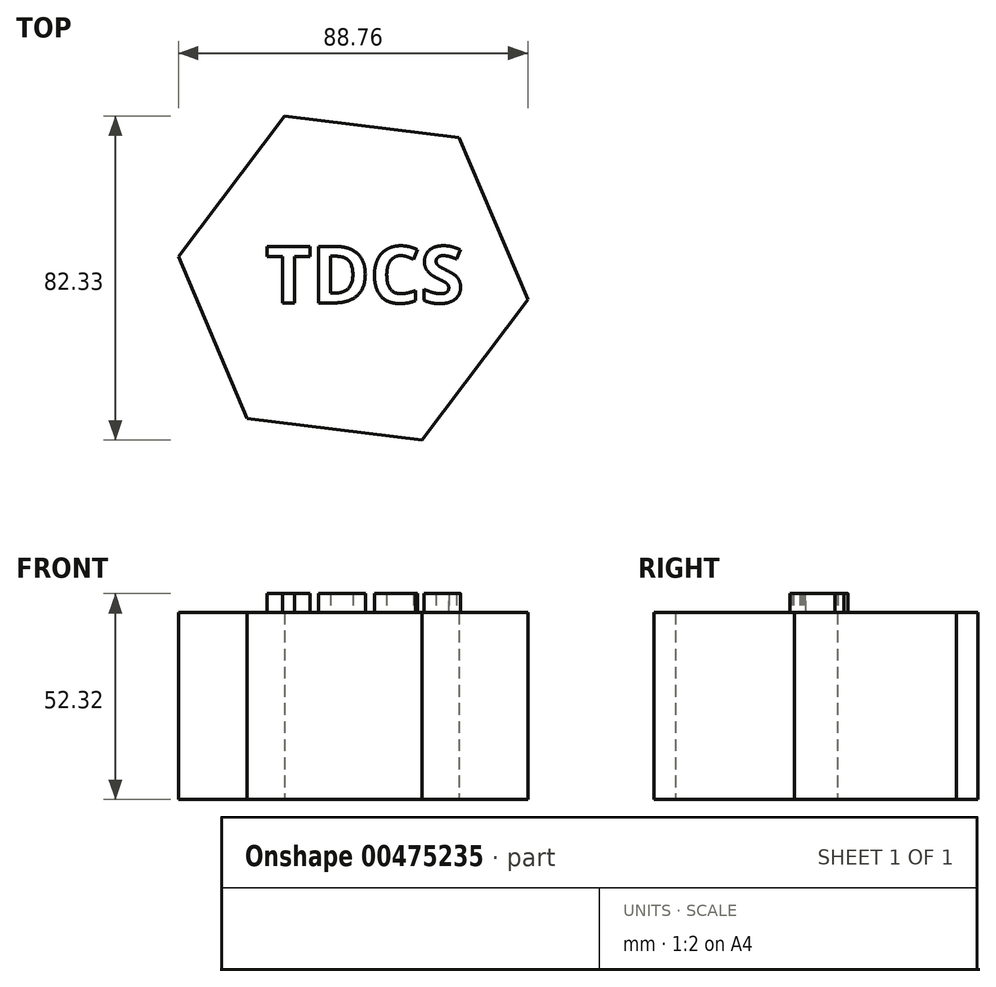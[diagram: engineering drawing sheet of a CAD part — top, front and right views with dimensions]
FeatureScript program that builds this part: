
annotation { "Feature Type Name" : "Feature", "Feature Type Description" : "" }
export const myFeature = defineFeature(function(context is Context, id is Id, definition is map)
    precondition{}
    {
        {
            var Q0;
            Q0=qCreatedBy(makeId("Top.planeOp"),FACE);
            var sketch = newSketch(context, id + "F0", { "sketchPlane" : qUnion([Q0])});
            skCircle(sketch, "E0.cCircle", {"center": v(-33.68, 25.98) * mm, "radius": 38.73 * mm, "construction": true});
            skLineSegment(sketch, "E0.0", {"start": v(10.7, 20.51) * mm, "end": v(-16.22, -15.2) * mm});
            skLineSegment(sketch, "E0.1", {"start": v(-16.22, -15.2) * mm, "end": v(-60.6, -9.73) * mm});
            skLineSegment(sketch, "E0.2", {"start": v(-60.6, -9.73) * mm, "end": v(-78.06, 31.44) * mm});
            skLineSegment(sketch, "E0.3", {"start": v(-78.06, 31.44) * mm, "end": v(-51.14, 67.14) * mm});
            skLineSegment(sketch, "E0.4", {"start": v(-51.14, 67.14) * mm, "end": v(-6.76, 61.68) * mm});
            skLineSegment(sketch, "E0.5", {"start": v(-6.76, 61.68) * mm, "end": v(10.7, 20.51) * mm});
            skPoint(sketch, "E0.0.midPoint", {"position": v(-2.76, 2.66) * mm});
            skSolve(sketch);
        }
        {
            var Q0;
            Q0=makeQuery(id+"F0.imprint","IMPRINT",FACE,{"disambiguationData":[TD([[makeQuery(id+"F0.imprint","IMPRINT",EDGE,{"derivedFrom":sQuery(id+"F0.wireOp",EDGE,"E0.0")}),-1.0]])]});
            extrude(context, id + "F1", {"entities" : qUnion([Q0]), "depth" : 47.5 * mm});
        }
        {
            var Q0;
            Q0=makeQuery(id+"F1.opExtrude","CAP_FACE",FACE,{"disambiguationData":[OSD([sQuery(id+"F0.wireOp",EDGE,"E0.0"),sQuery(id+"F0.wireOp",EDGE,"E0.1"),sQuery(id+"F0.wireOp",EDGE,"E0.2"),sQuery(id+"F0.wireOp",EDGE,"E0.3"),sQuery(id+"F0.wireOp",EDGE,"E0.4"),sQuery(id+"F0.wireOp",EDGE,"E0.5")])],"isStart":false});
            var sketch = newSketch(context, id + "F2", { "sketchPlane" : qUnion([Q0])});
            skText(sketch, "E1", { "text": "TDCS", "fontName": "OpenSans-Bold.ttf"});
            const initialGuessF2  = {"E1": [-0.05588, 0.01967, 1, 0, 0.01444]};
            skSetInitialGuess(sketch, initialGuessF2);
            skSolve(sketch);
        }
        {
            var Q0;
            Q0 = qSketchRegion(id + "F2", true);
            extrude(context, id + "F3", {"entities" : qUnion([Q0]), "operationType" : NewBodyOperationType.ADD, "depth" : 4.83 * mm});
        }
    });
